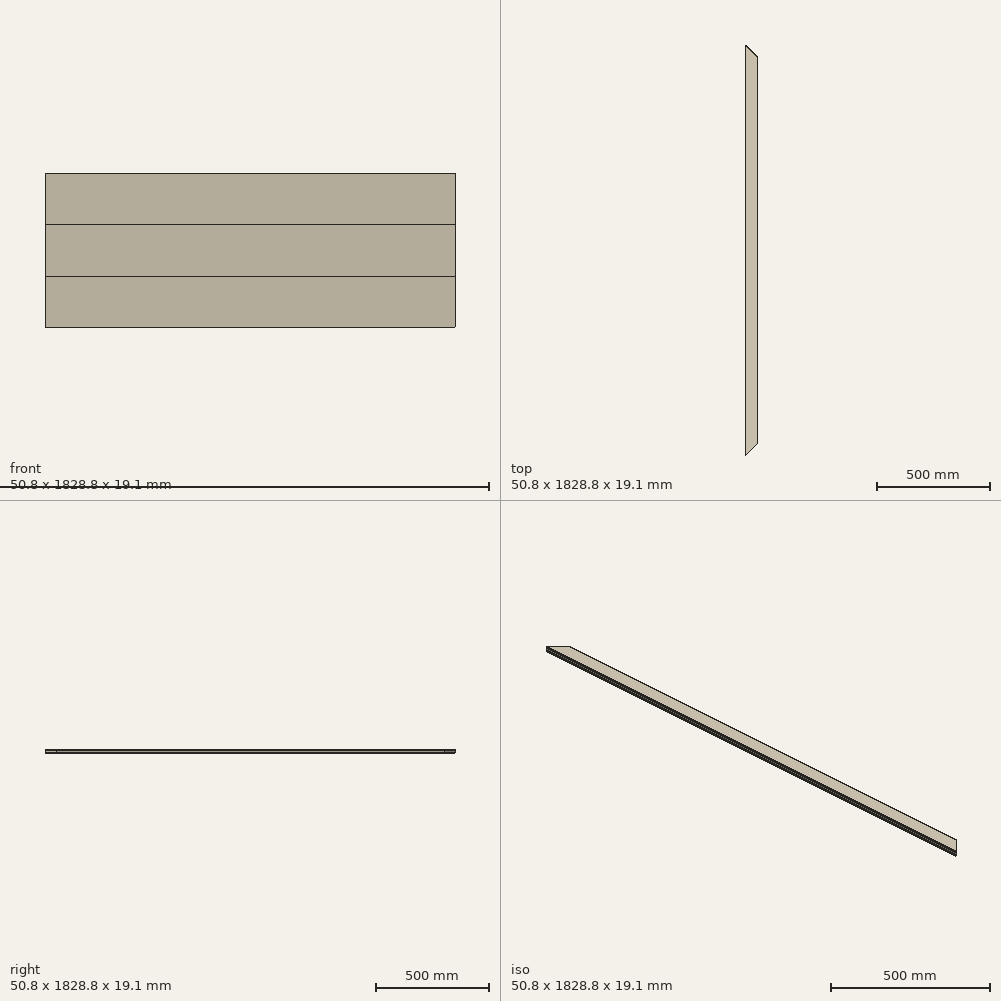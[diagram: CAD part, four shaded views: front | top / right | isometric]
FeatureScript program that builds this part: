
annotation { "Feature Type Name" : "Feature", "Feature Type Description" : "" }
export const myFeature = defineFeature(function(context is Context, id is Id, definition is map)
    precondition{}
    {
        {
            var Q0;
            Q0=qCreatedBy(makeId("Top.planeOp"),FACE);
            var sketch = newSketch(context, id + "F0", { "sketchPlane" : qUnion([Q0])});
            skLineSegment(sketch, "E0.bottom", {"start": v(-1201.92, -78.8) * mm, "end": v(17.28, -78.8) * mm});
            skLineSegment(sketch, "E0.top", {"start": v(-1201.92, -688.4) * mm, "end": v(17.28, -688.4) * mm});
            skLineSegment(sketch, "E0.left", {"start": v(-1201.92, -78.8) * mm, "end": v(-1201.92, -688.4) * mm});
            skLineSegment(sketch, "E0.right", {"start": v(17.28, -78.8) * mm, "end": v(17.28, -688.4) * mm});
            skLineSegment(sketch, "E1.top", {"start": v(-1174.85, -813.1) * mm, "end": v(-565.25, -813.1) * mm});
            skLineSegment(sketch, "E1.left", {"start": v(-1174.85, -813.1) * mm, "end": v(-1174.85, -2641.9) * mm});
            skLineSegment(sketch, "E1.right", {"start": v(-565.25, -813.1) * mm, "end": v(-565.25, -2641.9) * mm});
            skLineSegment(sketch, "E2.bottom", {"start": v(-2751.32, -78.94) * mm, "end": v(-1532.12, -78.94) * mm});
            skLineSegment(sketch, "E2.top", {"start": v(-2751.32, -2517.34) * mm, "end": v(-1532.12, -2517.34) * mm});
            skLineSegment(sketch, "E2.left", {"start": v(-2751.32, -78.94) * mm, "end": v(-2751.32, -2517.34) * mm});
            skLineSegment(sketch, "E2.right", {"start": v(-1532.12, -78.94) * mm, "end": v(-1532.12, -2517.34) * mm});
            skLineSegment(sketch, "E3", {"start": v(-1124.05, -863.9) * mm, "end": v(-1124.05, -2591.1) * mm});
            skPoint(sketch, "E4", {"position": v(-1124.05, -863.9) * mm});
            skLineSegment(sketch, "E5", {"start": v(-1124.05, -863.9) * mm, "end": v(-1174.85, -813.1) * mm});
            skPoint(sketch, "E6", {"position": v(-1124.05, -2591.1) * mm});
            skLineSegment(sketch, "E7", {"start": v(-1124.05, -2591.1) * mm, "end": v(-1174.85, -2641.9) * mm});
            skSolve(sketch);
        }
        {
            var Q0;
            Q0=makeQuery(id+"F0.imprint","IMPRINT",FACE,{"disambiguationData":[TD([[makeQuery(id+"F0.imprint","IMPRINT",EDGE,{"derivedFrom":sQuery(id+"F0.wireOp",EDGE,"E1.left")}),1.0]])]});
            extrude(context, id + "F1", {"entities" : qUnion([Q0]), "depth" : 6.35 * mm});
        }
        {
            var Q0;
            Q0=makeQuery(id+"F1.opExtrude","CAP_FACE",FACE,{"disambiguationData":[OSD([sQuery(id+"F0.wireOp",EDGE,"E1.left"),sQuery(id+"F0.wireOp",EDGE,"E3"),sQuery(id+"F0.wireOp",EDGE,"E5"),sQuery(id+"F0.wireOp",EDGE,"E7")])],"isStart":false});
            var sketch = newSketch(context, id + "F2", { "sketchPlane" : qUnion([Q0])});
            skLineSegment(sketch, "E8.0.0", {"start": v(-1124.05, -2591.1) * mm, "end": v(-1124.05, -863.9) * mm});
            skLineSegment(sketch, "E8.0.1", {"start": v(-1124.05, -863.9) * mm, "end": v(-1174.85, -813.1) * mm});
            skLineSegment(sketch, "E8.0.2", {"start": v(-1174.85, -813.1) * mm, "end": v(-1174.85, -2641.9) * mm});
            skLineSegment(sketch, "E8.0.3", {"start": v(-1174.85, -2641.9) * mm, "end": v(-1124.05, -2591.1) * mm});
            skSolve(sketch);
        }
        {
            var Q0;
            Q0=makeQuery(id+"F2.imprint","IMPRINT",FACE,{"disambiguationData":[TD([[makeQuery(id+"F2.imprint","IMPRINT",EDGE,{"derivedFrom":sQuery(id+"F2.wireOp",EDGE,"E8.0.0")}),-1.0]])]});
            var sketch = newSketch(context, id + "F3", { "sketchPlane" : qUnion([Q0])});
            skLineSegment(sketch, "E9.0.0", {"start": v(-1124.05, -2591.1) * mm, "end": v(-1124.05, -863.9) * mm});
            skLineSegment(sketch, "E9.0.1", {"start": v(-1124.05, -863.9) * mm, "end": v(-1174.85, -813.1) * mm});
            skLineSegment(sketch, "E9.0.2", {"start": v(-1174.85, -813.1) * mm, "end": v(-1174.85, -2641.9) * mm});
            skLineSegment(sketch, "E9.0.3", {"start": v(-1174.85, -2641.9) * mm, "end": v(-1124.05, -2591.1) * mm});
            skSolve(sketch);
        }
        {
            var Q0;
            Q0 = qSketchRegion(id + "F3", true);
            extrude(context, id + "F4", {"entities" : qUnion([Q0]), "depth" : 6.35 * mm});
        }
        {
            var Q0;
            Q0=makeQuery(id+"F4.opExtrude","CAP_FACE",FACE,{"disambiguationData":[OSD([sQuery(id+"F3.wireOp",EDGE,"E9.0.0"),sQuery(id+"F3.wireOp",EDGE,"E9.0.1"),sQuery(id+"F3.wireOp",EDGE,"E9.0.2"),sQuery(id+"F3.wireOp",EDGE,"E9.0.3")])],"isStart":false});
            var sketch = newSketch(context, id + "F5", { "sketchPlane" : qUnion([Q0])});
            skLineSegment(sketch, "E10.0.0", {"start": v(-1124.05, -2591.1) * mm, "end": v(-1124.05, -863.9) * mm});
            skLineSegment(sketch, "E10.0.1", {"start": v(-1124.05, -863.9) * mm, "end": v(-1174.85, -813.1) * mm});
            skLineSegment(sketch, "E10.0.2", {"start": v(-1174.85, -813.1) * mm, "end": v(-1174.85, -2641.9) * mm});
            skLineSegment(sketch, "E10.0.3", {"start": v(-1174.85, -2641.9) * mm, "end": v(-1124.05, -2591.1) * mm});
            skSolve(sketch);
        }
        {
            var Q0;
            Q0 = qSketchRegion(id + "F5", true);
            extrude(context, id + "F6", {"entities" : qUnion([Q0]), "depth" : 6.35 * mm});
        }
    });
